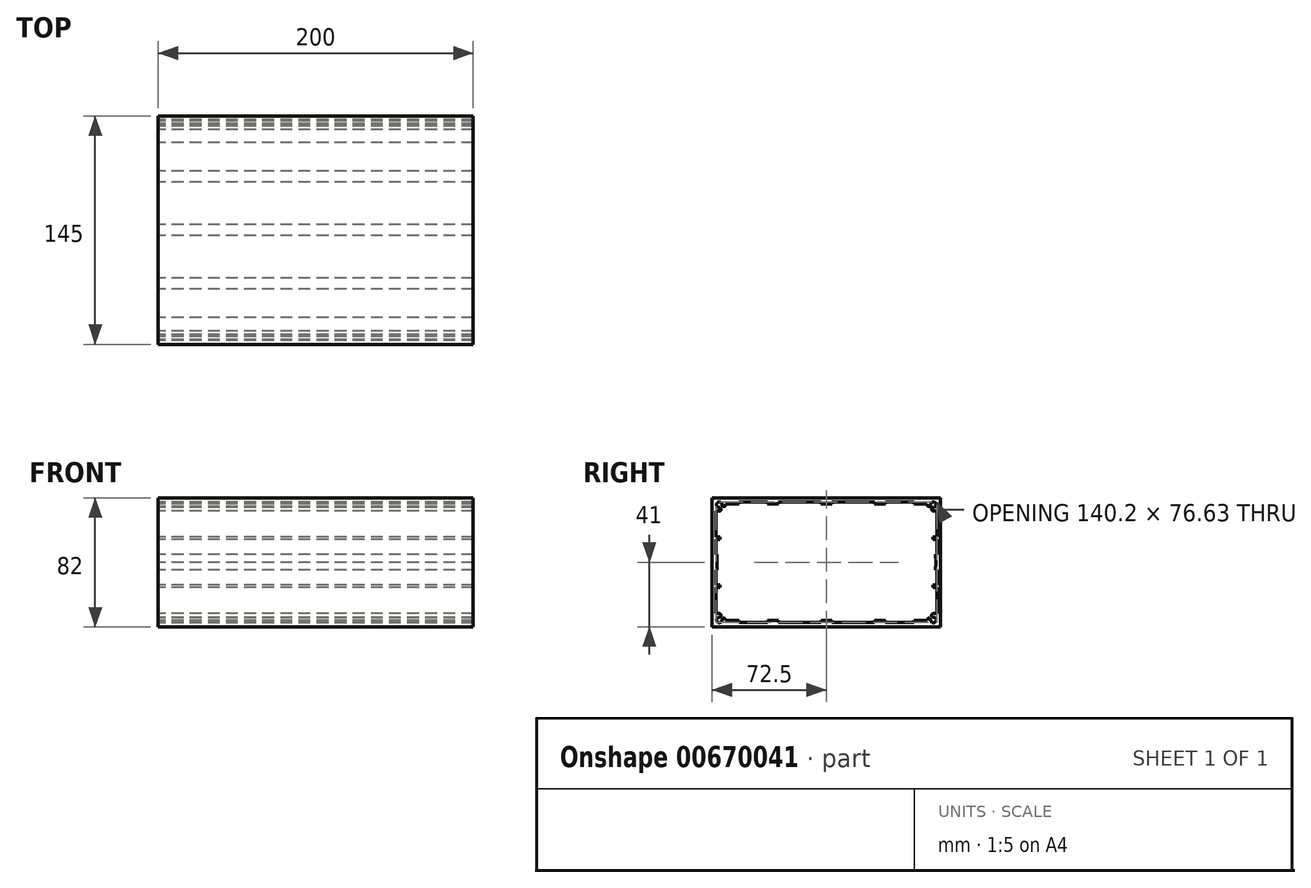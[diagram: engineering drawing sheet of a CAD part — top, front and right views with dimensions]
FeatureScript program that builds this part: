
annotation { "Feature Type Name" : "Feature", "Feature Type Description" : "" }
export const myFeature = defineFeature(function(context is Context, id is Id, definition is map)
    precondition{}
    {
        {
            var Q0;
            Q0=qCreatedBy(makeId("Right.planeOp"),FACE);
            var sketch = newSketch(context, id + "F0", { "sketchPlane" : qUnion([Q0])});
            skLineSegment(sketch, "E0.bottom", {"start": v(0, 0) * mm, "end": v(145, 0) * mm});
            skLineSegment(sketch, "E0.top", {"start": v(0, 82) * mm, "end": v(145, 82) * mm});
            skLineSegment(sketch, "E0.left", {"start": v(0, 0) * mm, "end": v(0, 82) * mm});
            skLineSegment(sketch, "E0.right", {"start": v(145, 0) * mm, "end": v(145, 82) * mm});
            skLineSegment(sketch, "E1", {"start": v(72.5, 82) * mm, "end": v(72.5, 0) * mm, "construction": true});
            skLineSegment(sketch, "E2", {"start": v(0, 41) * mm, "end": v(145, 41) * mm, "construction": true});
            skPoint(sketch, "E3.middle", {"position": v(72.5, 41) * mm});
            skLineSegment(sketch, "E4", {"start": v(72.5, 78) * mm, "end": v(69, 78) * mm});
            skLineSegment(sketch, "E5", {"start": v(69, 78) * mm, "end": v(69, 79.3) * mm});
            skLineSegment(sketch, "E6", {"start": v(69, 79.3) * mm, "end": v(42, 79.3) * mm});
            skLineSegment(sketch, "E7", {"start": v(42, 79.3) * mm, "end": v(42, 78) * mm});
            skLineSegment(sketch, "E8", {"start": v(42, 78) * mm, "end": v(35, 78) * mm});
            skLineSegment(sketch, "E9", {"start": v(35, 78) * mm, "end": v(35, 79.3) * mm});
            skLineSegment(sketch, "E10", {"start": v(35, 79.3) * mm, "end": v(17, 79.3) * mm});
            skLineSegment(sketch, "E11", {"start": v(17, 79.3) * mm, "end": v(17, 78) * mm});
            skLineSegment(sketch, "E12", {"start": v(17, 78) * mm, "end": v(8.55, 78) * mm});
            skArc(sketch, "E13", {"start": v(6.25, 77.6) * mm, "mid": v(3.26, 78.84) * mm, "end": v(4.5, 75.85) * mm});
            skArc(sketch, "E14", {"start": v(6.25, 77.6) * mm, "mid": v(7.4, 76.45) * mm, "end": v(8.55, 77.6) * mm});
            skLineSegment(sketch, "E15", {"start": v(8.55, 77.6) * mm, "end": v(8.55, 78) * mm});
            skArc(sketch, "E16", {"start": v(4.5, 73.55) * mm, "mid": v(5.65, 74.7) * mm, "end": v(4.5, 75.85) * mm});
            skLineSegment(sketch, "E17", {"start": v(4.5, 73.55) * mm, "end": v(2.4, 73.55) * mm});
            skLineSegment(sketch, "E18", {"start": v(2.4, 73.55) * mm, "end": v(2.4, 57) * mm});
            skLineSegment(sketch, "E19", {"start": v(2.4, 57) * mm, "end": v(4.92, 57) * mm});
            skLineSegment(sketch, "E20", {"start": v(4.92, 57) * mm, "end": v(4.92, 55.5) * mm});
            skLineSegment(sketch, "E21", {"start": v(4.92, 55.5) * mm, "end": v(2.4, 55.5) * mm});
            skLineSegment(sketch, "E22", {"start": v(2.4, 55.5) * mm, "end": v(2.4, 45.97) * mm});
            skLineSegment(sketch, "E23", {"start": v(2.4, 45.97) * mm, "end": v(3.13, 45.97) * mm});
            skLineSegment(sketch, "E24", {"start": v(3.13, 45.97) * mm, "end": v(3, 41) * mm});
            skLineSegment(sketch, "E25.MirrorCS", {"start": v(103, 79.3) * mm, "end": v(103, 78) * mm});
            skLineSegment(sketch, "E26.MirrorCS", {"start": v(142.6, 45.97) * mm, "end": v(141.87, 45.97) * mm});
            skLineSegment(sketch, "E27.MirrorCS", {"start": v(110, 78) * mm, "end": v(110, 79.3) * mm});
            skLineSegment(sketch, "E28.MirrorCS", {"start": v(128, 79.3) * mm, "end": v(128, 78) * mm});
            skLineSegment(sketch, "E29.MirrorCS", {"start": v(140.08, 55.5) * mm, "end": v(142.6, 55.5) * mm});
            skLineSegment(sketch, "E30.MirrorCS", {"start": v(140.08, 57) * mm, "end": v(140.08, 55.5) * mm});
            skLineSegment(sketch, "E31.MirrorCS", {"start": v(76, 78) * mm, "end": v(76, 79.3) * mm});
            skLineSegment(sketch, "E32.MirrorCS", {"start": v(136.45, 77.6) * mm, "end": v(136.45, 78) * mm});
            skLineSegment(sketch, "E33.MirrorCS", {"start": v(142.6, 73.55) * mm, "end": v(142.6, 57) * mm});
            skLineSegment(sketch, "E34.MirrorCS", {"start": v(140.5, 73.55) * mm, "end": v(142.6, 73.55) * mm});
            skLineSegment(sketch, "E35.MirrorCS", {"start": v(142.6, 55.5) * mm, "end": v(142.6, 45.97) * mm});
            skArc(sketch, "E36.MirrorCS", {"start": v(138.75, 77.6) * mm, "mid": v(137.6, 76.45) * mm, "end": v(136.45, 77.6) * mm});
            skLineSegment(sketch, "E37.MirrorCS", {"start": v(142.6, 57) * mm, "end": v(140.08, 57) * mm});
            skLineSegment(sketch, "E38.MirrorCS", {"start": v(110, 79.3) * mm, "end": v(128, 79.3) * mm});
            skLineSegment(sketch, "E39.MirrorCS", {"start": v(141.87, 45.97) * mm, "end": v(142, 41) * mm});
            skLineSegment(sketch, "E40.MirrorCS", {"start": v(128, 78) * mm, "end": v(136.45, 78) * mm});
            skLineSegment(sketch, "E41.MirrorCS", {"start": v(76, 79.3) * mm, "end": v(103, 79.3) * mm});
            skLineSegment(sketch, "E42.MirrorCS", {"start": v(72.5, 78) * mm, "end": v(76, 78) * mm});
            skLineSegment(sketch, "E43.MirrorCS", {"start": v(103, 78) * mm, "end": v(110, 78) * mm});
            skArc(sketch, "E44.MirrorCS", {"start": v(138.75, 77.6) * mm, "mid": v(141.74, 78.84) * mm, "end": v(140.5, 75.85) * mm});
            skArc(sketch, "E45.MirrorCS", {"start": v(140.5, 73.55) * mm, "mid": v(139.35, 74.7) * mm, "end": v(140.5, 75.85) * mm});
            skLineSegment(sketch, "E46.MirrorCS", {"start": v(2.4, 8.45) * mm, "end": v(2.4, 25) * mm});
            skLineSegment(sketch, "E47.MirrorCS", {"start": v(4.5, 8.45) * mm, "end": v(2.4, 8.45) * mm});
            skLineSegment(sketch, "E48.MirrorCS", {"start": v(5, 19.2) * mm, "end": v(5, 19.21) * mm});
            skArc(sketch, "E49.MirrorCS", {"start": v(138.75, 4.4) * mm, "mid": v(137.6, 5.55) * mm, "end": v(136.45, 4.4) * mm});
            skLineSegment(sketch, "E50.MirrorCS", {"start": v(8.55, 4.4) * mm, "end": v(8.55, 4) * mm});
            skLineSegment(sketch, "E51.MirrorCS", {"start": v(136.45, 4.4) * mm, "end": v(136.45, 4) * mm});
            skLineSegment(sketch, "E52.MirrorCS", {"start": v(72.5, 4) * mm, "end": v(69, 4) * mm});
            skArc(sketch, "E53.MirrorCS", {"start": v(6.25, 4.4) * mm, "mid": v(7.4, 5.55) * mm, "end": v(8.55, 4.4) * mm});
            skLineSegment(sketch, "E54.MirrorCS", {"start": v(69, 4) * mm, "end": v(69, 2.7) * mm});
            skLineSegment(sketch, "E55.MirrorCS", {"start": v(142.6, 25) * mm, "end": v(140.08, 25) * mm});
            skLineSegment(sketch, "E56.MirrorCS", {"start": v(4.92, 26.5) * mm, "end": v(2.4, 26.5) * mm});
            skArc(sketch, "E57.MirrorCS", {"start": v(4.5, 8.45) * mm, "mid": v(5.65, 7.3) * mm, "end": v(4.5, 6.15) * mm});
            skLineSegment(sketch, "E58.MirrorCS", {"start": v(140.08, 25) * mm, "end": v(140.08, 26.5) * mm});
            skLineSegment(sketch, "E59.MirrorCS", {"start": v(2.4, 36.03) * mm, "end": v(3.13, 36.03) * mm});
            skLineSegment(sketch, "E60.MirrorCS", {"start": v(4.92, 25) * mm, "end": v(4.92, 26.5) * mm});
            skLineSegment(sketch, "E61.MirrorCS", {"start": v(140.5, 8.45) * mm, "end": v(142.6, 8.45) * mm});
            skLineSegment(sketch, "E62.MirrorCS", {"start": v(140.08, 26.5) * mm, "end": v(142.6, 26.5) * mm});
            skLineSegment(sketch, "E63.MirrorCS", {"start": v(72.5, 4) * mm, "end": v(76, 4) * mm});
            skLineSegment(sketch, "E64.MirrorCS", {"start": v(142.6, 8.45) * mm, "end": v(142.6, 25) * mm});
            skLineSegment(sketch, "E65.MirrorCS", {"start": v(2.4, 25) * mm, "end": v(4.92, 25) * mm});
            skLineSegment(sketch, "E66.MirrorCS", {"start": v(128, 2.7) * mm, "end": v(128, 4) * mm});
            skLineSegment(sketch, "E67.MirrorCS", {"start": v(2.4, 26.5) * mm, "end": v(2.4, 36.03) * mm});
            skLineSegment(sketch, "E68.MirrorCS", {"start": v(103, 2.7) * mm, "end": v(103, 4) * mm});
            skLineSegment(sketch, "E69.MirrorCS", {"start": v(42, 2.7) * mm, "end": v(42, 4) * mm});
            skLineSegment(sketch, "E70.MirrorCS", {"start": v(142.6, 36.03) * mm, "end": v(141.87, 36.03) * mm});
            skLineSegment(sketch, "E71.MirrorCS", {"start": v(76, 4) * mm, "end": v(76, 2.7) * mm});
            skLineSegment(sketch, "E72.MirrorCS", {"start": v(17, 2.7) * mm, "end": v(17, 4) * mm});
            skLineSegment(sketch, "E73.MirrorCS", {"start": v(110, 4) * mm, "end": v(110, 2.7) * mm});
            skLineSegment(sketch, "E74.MirrorCS", {"start": v(142.6, 26.5) * mm, "end": v(142.6, 36.03) * mm});
            skArc(sketch, "E75.MirrorCS", {"start": v(140.5, 8.45) * mm, "mid": v(139.35, 7.3) * mm, "end": v(140.5, 6.15) * mm});
            skLineSegment(sketch, "E76.MirrorCS", {"start": v(35, 4) * mm, "end": v(35, 2.7) * mm});
            skArc(sketch, "E77.MirrorCS", {"start": v(6.25, 4.4) * mm, "mid": v(3.26, 3.16) * mm, "end": v(4.5, 6.15) * mm});
            skArc(sketch, "E78.MirrorCS", {"start": v(138.75, 4.4) * mm, "mid": v(141.74, 3.16) * mm, "end": v(140.5, 6.15) * mm});
            skLineSegment(sketch, "E79.MirrorCS", {"start": v(3.13, 36.03) * mm, "end": v(3, 41) * mm});
            skLineSegment(sketch, "E80.MirrorCS", {"start": v(141.87, 36.03) * mm, "end": v(142, 41) * mm});
            skLineSegment(sketch, "E81.MirrorCS", {"start": v(17, 4) * mm, "end": v(8.55, 4) * mm});
            skLineSegment(sketch, "E82.MirrorCS", {"start": v(128, 4) * mm, "end": v(136.45, 4) * mm});
            skLineSegment(sketch, "E83.MirrorCS", {"start": v(103, 4) * mm, "end": v(110, 4) * mm});
            skLineSegment(sketch, "E84.MirrorCS", {"start": v(76, 2.7) * mm, "end": v(103, 2.7) * mm});
            skLineSegment(sketch, "E85.MirrorCS", {"start": v(42, 4) * mm, "end": v(35, 4) * mm});
            skLineSegment(sketch, "E86.MirrorCS", {"start": v(35, 2.7) * mm, "end": v(17, 2.7) * mm});
            skLineSegment(sketch, "E87.MirrorCS", {"start": v(110, 2.7) * mm, "end": v(128, 2.7) * mm});
            skLineSegment(sketch, "E88.MirrorCS", {"start": v(69, 2.7) * mm, "end": v(42, 2.7) * mm});
            skSolve(sketch);
        }
        {
            var Q0;
            Q0=qSketchRegion(id+"F0",true);
            extrude(context, id + "F1", {"entities" : qUnion([Q0]), "depth" : 200 * mm, "offsetDistance" : 25 * mm});
        }
    });
